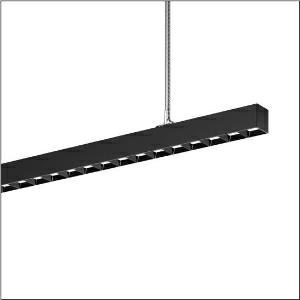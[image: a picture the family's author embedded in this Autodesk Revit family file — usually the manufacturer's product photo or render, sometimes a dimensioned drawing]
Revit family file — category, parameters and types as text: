
# Revit family: silica_r__21_51mx31dc4dbb_76cd
name_source: partatom
category: Lighting Fixtures
units: mm (PartAtom-declared; Revit-internal decimal feet)

## family parameters
Cut with Voids When Loaded = No
Host = Face
Light Source = No
Part Type = Normal
Room Calculation Point = No
Round Connector Dimension = Use Diameter
Shared = No

## types (1)
- --- (1 x LED, 18230 lm, 105.9 W, 4000K)
    Apparent Load = 106 VA
    CIE Flux Codes = 87 99 100 59 100
    Color Rendering = 80
    Color Temperature = 4000K
    Default Elevation = 1800 mm
    Description = Silica® 21, office luminaire, primary light control with darklight reflector, of PMMA, black, CAT 2 (L<= 3000cd/m²), light emission: direct/indirect distribution, primary light characteristic: symmetric, installation type: suspended mounting, LED, rated luminous flux: 18.230lm, luminous efficacy: 172lm/W, light colour: 840, colour temperature: 4000K, with terminal, 3+2-pole, max. 2.5mm², mains connection: 220..240V, AC, 50/60Hz, rated input power: 105.9W, luminaire housing, of aluminium, jet black (RAL 9005), length: 3.004mm, width: 53mm, height: 53mm, protection rating (complete): IP20, insulation class (complete): insulation class I (protective earthing), certification: CE, permissible operating ambient temperature: 0..+35°C, standard: EN 50419, packaging unit: 1 piece
    Height = 53 mm
    Lamp = 1 x LED
    Lamp Light Flux = 18230 lm
    Lamp Power = 105.9 W
    Lamp count = 1
    Length = 3004 mm
    Luminous efficacy = 172 lm/W
    Manufacturer = Siteco
    ModVariant = No
    Model = 51MX31DC4DBB
    Mounting Place = Ceiling
    Mounting Type = Pendant
    Number of Poles = 1
    OnlyDefault = Yes
    Power Factor = 1
    Product Name = Silica® 21
    Product group = office luminaire | ceiling pendant
    ProductGroupID = 902
    Protection Class = Protection class I
    Protection Degree = IP 20
    RLX_Detail_Level = 1
    RLX_Emergency_Light_Flux = 0 lm
    RLX_Emergency_Type = 0
    RLX_Emergency_Type_DB = No
    RlxData = <blob elided: 66601 chars, md5=e2c752b8>
    Socket = socket
    Standby Power = 0 W
    System Light Flux = 18230 lm
    System Power = 106 W
    Type Comments = factory setting: luminous flux: 100 % | dim-lin: 254 | 367 mA
    Type Image = l_1313617.jpg
    URL = http://relux.com
    VarID = @adj_069955
    Voltage = 0 V
    Weight = 0.00 kg
    Width = 53 mm

## geometry (parser evidence)
native form markers: Blend x4, Sweep x12
no freeform markers — native parametric forms only
